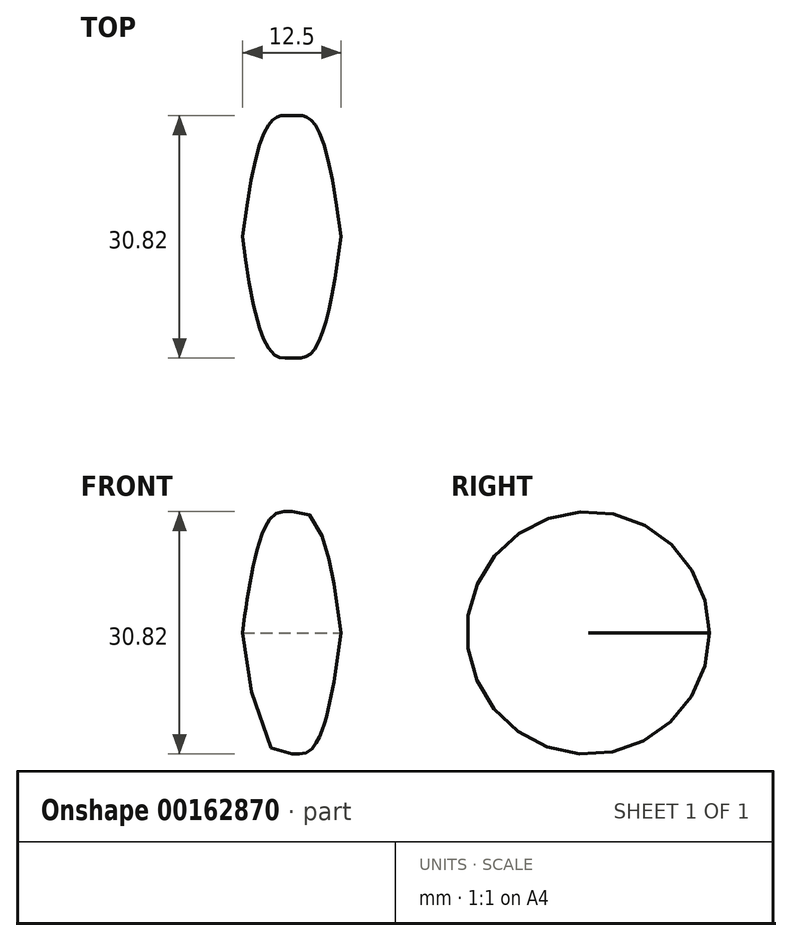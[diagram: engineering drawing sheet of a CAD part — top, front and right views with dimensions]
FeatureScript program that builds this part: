
annotation { "Feature Type Name" : "Feature", "Feature Type Description" : "" }
export const myFeature = defineFeature(function(context is Context, id is Id, definition is map)
    precondition{}
    {
        {
            var Q0;
            Q0=qCreatedBy(makeId("Top.planeOp"),FACE);
            var sketch = newSketch(context, id + "F0", { "sketchPlane" : qUnion([Q0])});
            skPoint(sketch, "E0", {"position": v(-6.25, 0) * mm});
            skPoint(sketch, "E1", {"position": v(0, 15.38) * mm});
            skPoint(sketch, "E2", {"position": v(6.25, 0) * mm});
            skFitSpline(sketch, "E3", {"points": [v(-6.25, 0) * mm, v(0, 15.38) * mm, v(6.25, 0) * mm], "startDerivative": vector(12.5, 100) * mm, "endDerivative": vector(12.5, -100) * mm});
            skLineSegment(sketch, "E4", {"start": v(-6.25, 0) * mm, "end": v(6.25, 0) * mm});
            skSolve(sketch);
        }
        {
            var Q0;
            Q0=qSketchRegion(id+"F0",true);
            var Q1;
            Q1=sQuery(id+"F0.wireOp",EDGE,"E4");
            revolve(context, id + "F1", {"entities" : qUnion([Q0]), "axis" : qUnion([Q1]), "revolveType" : RevolveType.FULL});
        }
    });
